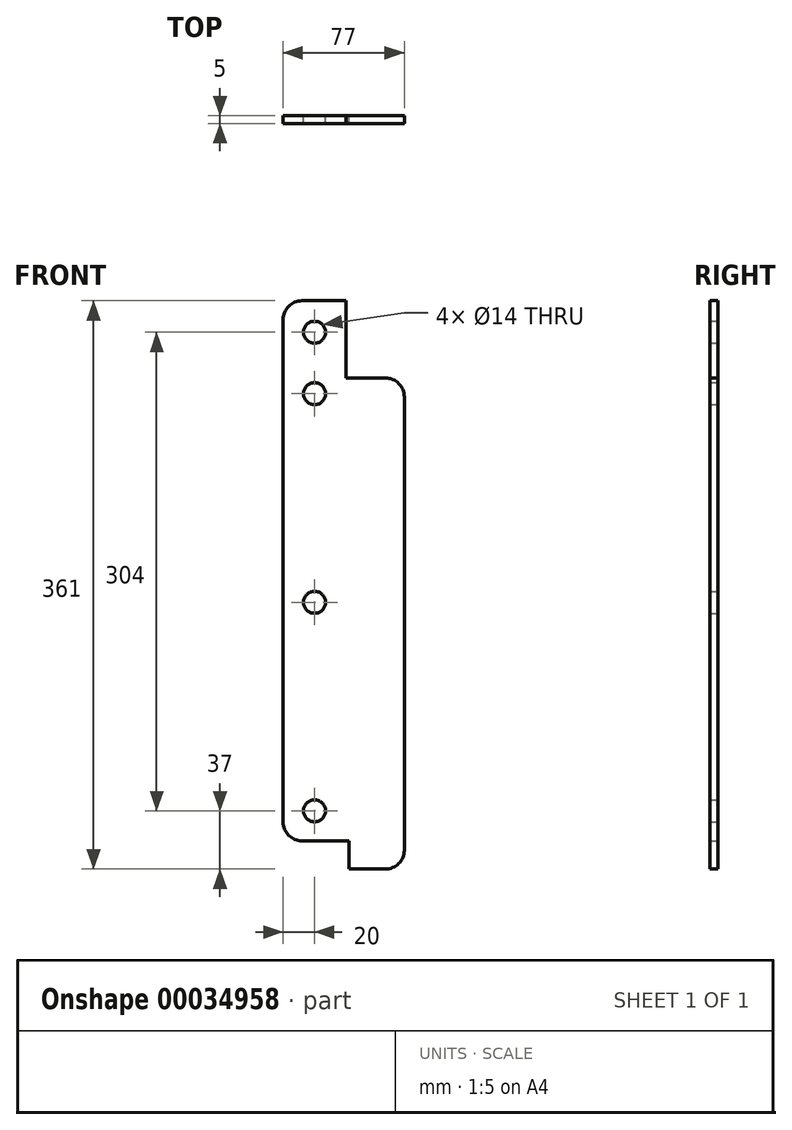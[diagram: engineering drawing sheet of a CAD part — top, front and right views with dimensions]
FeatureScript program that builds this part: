
annotation { "Feature Type Name" : "Feature", "Feature Type Description" : "" }
export const myFeature = defineFeature(function(context is Context, id is Id, definition is map)
    precondition{}
    {
        {
            var Q0;
            Q0=qCreatedBy(makeId("Front.planeOp"),FACE);
            var sketch = newSketch(context, id + "F0", { "sketchPlane" : qUnion([Q0])});
            skLineSegment(sketch, "E0", {"start": v(0, 12) * mm, "end": v(0, 331) * mm});
            skLineSegment(sketch, "E1", {"start": v(12, 343) * mm, "end": v(40, 343) * mm});
            skLineSegment(sketch, "E2", {"start": v(40, 343) * mm, "end": v(40, 294) * mm});
            skLineSegment(sketch, "E3", {"start": v(40, 294) * mm, "end": v(65, 294) * mm});
            skLineSegment(sketch, "E4", {"start": v(77, 282) * mm, "end": v(77, -6) * mm});
            skLineSegment(sketch, "E5", {"start": v(65, -18) * mm, "end": v(42, -18) * mm});
            skLineSegment(sketch, "E6", {"start": v(42, -18) * mm, "end": v(42, 0) * mm});
            skLineSegment(sketch, "E7", {"start": v(42, 0) * mm, "end": v(12, 0) * mm});
            skCircle(sketch, "E8", {"center": v(20, 323) * mm, "radius": 7 * mm});
            skPoint(sketch, "E8.centerSnap0", {"position": v(20, 343) * mm});
            skCircle(sketch, "E9", {"center": v(20, 284) * mm, "radius": 7 * mm});
            skCircle(sketch, "E10", {"center": v(20, 151.5) * mm, "radius": 7 * mm});
            skCircle(sketch, "E11", {"center": v(20, 19) * mm, "radius": 7 * mm});
            skPoint(sketch, "E12.visualSharp", {"position": v(0, 343) * mm});
            skArc(sketch, "E12.filletArc", {"start": v(12, 343) * mm, "mid": v(3.51, 339.49) * mm, "end": v(0, 331) * mm});
            skPoint(sketch, "E13.visualSharp", {"position": v(77, 294) * mm});
            skArc(sketch, "E13.filletArc", {"start": v(77, 282) * mm, "mid": v(73.49, 290.49) * mm, "end": v(65, 294) * mm});
            skPoint(sketch, "E14.visualSharp", {"position": v(77, -18) * mm});
            skArc(sketch, "E14.filletArc", {"start": v(65, -18) * mm, "mid": v(73.49, -14.49) * mm, "end": v(77, -6) * mm});
            skPoint(sketch, "E15.visualSharp", {"position": v(0, 0) * mm});
            skArc(sketch, "E15.filletArc", {"start": v(0, 12) * mm, "mid": v(3.51, 3.51) * mm, "end": v(12, 0) * mm});
            skSolve(sketch);
        }
        {
            var Q0;
            Q0=makeQuery(id+"F0.imprint","IMPRINT",FACE,{"disambiguationData":[TD([[makeQuery(id+"F0.imprint","IMPRINT",EDGE,{"derivedFrom":sQuery(id+"F0.wireOp",EDGE,"E0")}),-1.0]])]});
            extrude(context, id + "F1", {"entities" : qUnion([Q0]), "depth" : 5 * mm});
        }
    });
